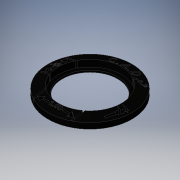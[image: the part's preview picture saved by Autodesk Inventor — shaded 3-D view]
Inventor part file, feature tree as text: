
AUTODESK INVENTOR PART (.ipt)
format: ipt  version: 2016 (Build 200138000, 138)  size: 792,576 bytes
history: native  units: in
note: dims shown in document units (in); Inventor stores cm internally (conversion verified against a paired STEP export)
features: reference x5, sketch x3, extrude x2, revolve x1, projected_geometry x1
ambient origin geometry x8: Origin, YZ Plane, XZ Plane, XY Plane, X Axis, Y Axis, Z Axis, Center Point
bodies: Solid1 (feature_tree)
feature tree (12):
  revolve  "Revolution1"  [1 undecoded]
  extrude  "Extrusion1"  Depth=0.1in
  extrude  "Extrusion2"  Depth=0.0175in
  sketch  "Sketch1"  dims[d0=0.8265in d1=0.175in]
  sketch  "Sketch2"  dims[d2=0.05in d3=0.1in]
  projected_geometry  "Projected Loop1"
  reference  "Reference1"
  reference  "Reference2"
  reference  "Reference3"
  sketch  "Sketch3"  dims[d4=0.15in d5=0.275in d6=90.0deg d7=1.55in d9=1.0in d11=0.035in d13=1.0in d14=0.035in d15=0.0175in d16=0.6536in d17=0.0175in d18=0.15in d19=0.075in d20=0.05in d21=0.035in d22=0.0175in d23=0.325in d24=0.0175in d25=0.15in d26=0.3in d27=0.1in d28=0.035in d29=0.015in d30=0.015in d31=0.035in d32=0.0175in d33=0.225in d34=0.1in d35=1.1in d36=0.035in d38=60.0deg d39=0.025in d40=0.0in d41=0.0in d42=0.125in d43=0.125in d44=0.04in d45=0.05in d46=0.04in d47=0.04in d49=0.025in d50=0.125in d51=0.5in d52=0.085in d53=0.1in d54=0.975in d55=0.025in d56=0.9812in d57=0.9812in d58=15.0deg d59=0.04in d60=0.025in d61=0.5in d62=0.0in]
  reference  "Reference4"
  reference  "Reference5"
note: 1 required parameter value undecoded (feature->parameter linkage not recoverable at this tier; creation-order binding heuristic only, values carry confidence <= 0.55)
